# Revit family: Tub_Spout-GROHE-Bauloop-13286000
name_source: partatom
category: Plumbing Fixtures
revit_build: Autodesk Revit 2018 (Build: 20170223_1515(x64)
units: mm (PartAtom-declared; Revit-internal decimal feet)

## family parameters
Cut with Voids When Loaded = Yes
Host = Face
OmniClass Number = 23.45.05.14.21.11
OmniClass Title = Bath/Shower Units
Part Type = Normal
Room Calculation Point = No
Round Connector Dimension = Use Diameter
Shared = Yes

## types (1)
- 13286000
    Assembly Code = D2090800
    CWFU = 3
    Connection Type = 1/2" NPT Inlet
    Default Elevation = 0"
    Description = Bauloop Tub Spout
    Finish = Metal-Grohe-000-Chrome
    Flow Rate = 6.9 gpm at 45 psi (26.1 L/min), 2.5 gpm (9.5 L/min) for Shower Hand
    HWFU = 3
    Height = 2 3/8"
    Installation Type = Wall mount slip fit installation
    Length = 5 3/16"
    Manufacturer = Grohe
    Material = Metal-Grohe-000-Chrome
    Model = 13286000
    Price = Prices may vary. Please consult Manufacturer Representative for most up-to-date price list.
    Product Documentation Link = https://americanstandard.box.com
    Product Page URL = https://www.grohe.us
    Revised Date = 19/04/2021
    Tempered Connection Diameter = 1/2"
    URL = https://www.grohe.us
    Vent Connection = No
    WFU = 4
    Warranty Documentation Link = https://cdn.cloud.grohe.com
    Waste Connection = No
    Width = 3 1/8"

## geometry (parser evidence)
native form markers: Sweep x3
no freeform markers — native parametric forms only
